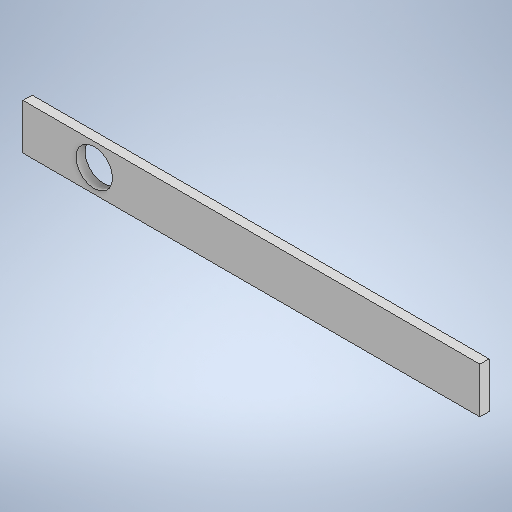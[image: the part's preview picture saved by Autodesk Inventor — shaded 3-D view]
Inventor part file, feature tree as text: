
AUTODESK INVENTOR PART (.ipt)
format: ipt  version: 2025.2 (Build 292293000, 293)  size: 226,816 bytes
history: native  units: mm
features: sketch x2, extrude x1, hole x1
ambient origin geometry x8: Origin, YZ Plane, XZ Plane, XY Plane, X Axis, Y Axis, Z Axis, Center Point
bodies: Solid1 (feature_tree)
feature tree (4):
  extrude  "Extrusion1"  Depth=10.0mm
  hole  "Hole1"  [1 undecoded]
  sketch  "Sketch1"  dims[d0=100.0mm d1=10.0mm]
  sketch  "Sketch2"  dims[d2=2.0mm d3=0.0mm d4=8.0mm d5=6.0mm d6=4.0mm d7=2.0mm d8=90.0deg d9=8.0mm d10=20.594885mm]
note: 1 required parameter value undecoded (feature->parameter linkage not recoverable at this tier; creation-order binding heuristic only, values carry confidence <= 0.55)
